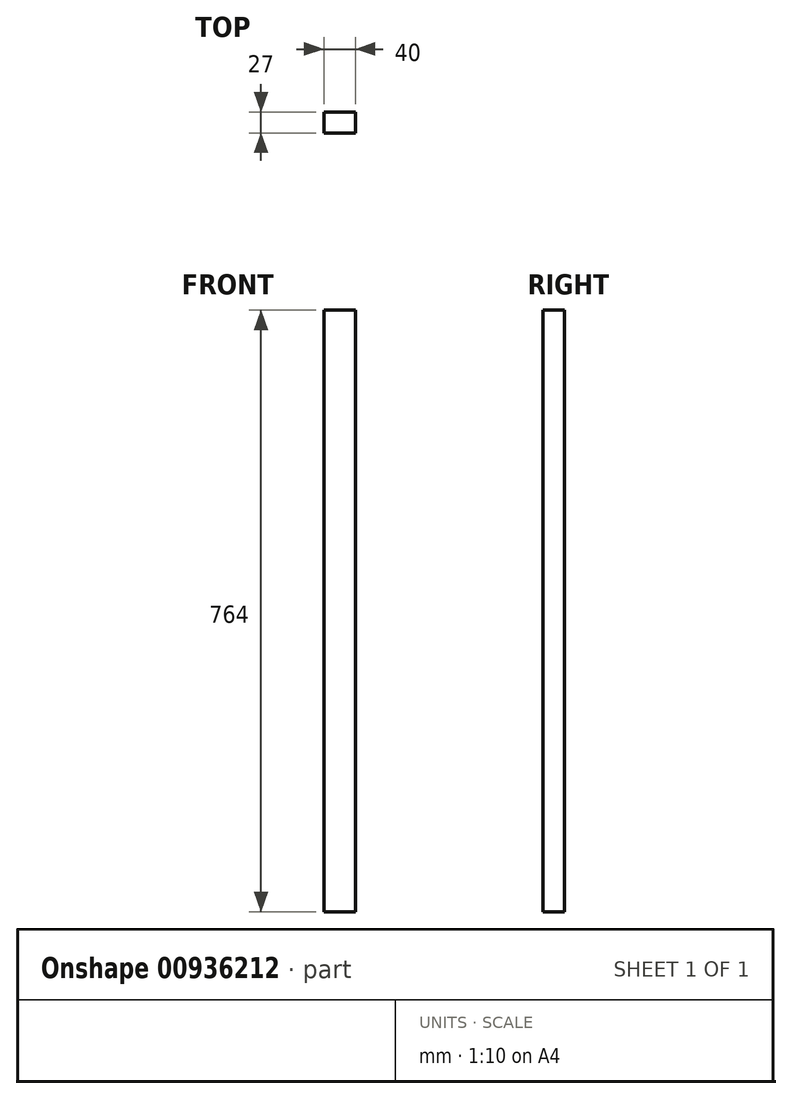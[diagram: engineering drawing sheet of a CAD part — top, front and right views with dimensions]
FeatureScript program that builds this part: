
annotation { "Feature Type Name" : "Feature", "Feature Type Description" : "" }
export const myFeature = defineFeature(function(context is Context, id is Id, definition is map)
    precondition{}
    {
        {
            var Q0;
            Q0=qCreatedBy(makeId("Top.planeOp"),FACE);
            var sketch = newSketch(context, id + "F0", { "sketchPlane" : qUnion([Q0])});
            skLineSegment(sketch, "E0.bottom", {"start": v(0, 0) * mm, "end": v(40, 0) * mm});
            skLineSegment(sketch, "E0.top", {"start": v(0, 27) * mm, "end": v(40, 27) * mm});
            skLineSegment(sketch, "E0.left", {"start": v(0, 0) * mm, "end": v(0, 27) * mm});
            skLineSegment(sketch, "E0.right", {"start": v(40, 0) * mm, "end": v(40, 27) * mm});
            skSolve(sketch);
        }
        {
            var Q0;
            Q0 = qSketchRegion(id + "F0", true);
            extrude(context, id + "F1", {"entities" : qUnion([Q0]), "depth" : 764 * mm, "offsetDistance" : 25 * mm});
        }
    });
